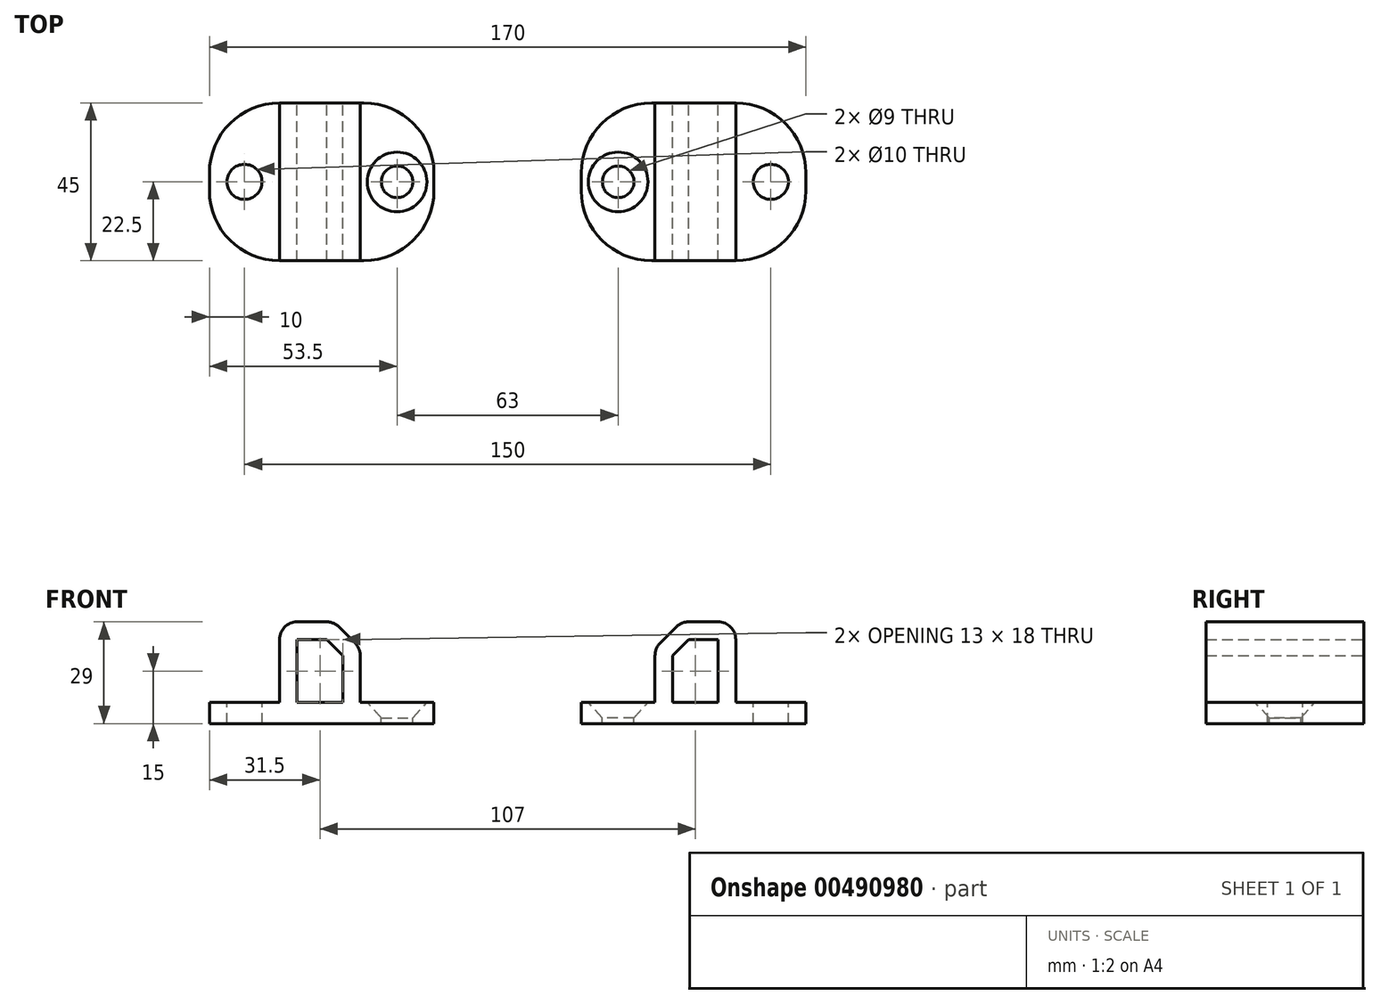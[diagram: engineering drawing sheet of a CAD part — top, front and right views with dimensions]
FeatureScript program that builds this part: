
annotation { "Feature Type Name" : "Feature", "Feature Type Description" : "" }
export const myFeature = defineFeature(function(context is Context, id is Id, definition is map)
    precondition{}
    {
        {
            var Q0;
            Q0=qCreatedBy(makeId("Front.planeOp"),FACE);
            cPlane(context, id + "F0", {"entities" : qUnion([Q0]), "cplaneType" : CPlaneType.OFFSET, "offset" : 15 * mm, "oppositeDirection" : true, "width" : 150 * mm, "height" : 150 * mm});
        }
        {
            var Q0;
            Q0=qCreatedBy(makeId("Top.planeOp"),FACE);
            cPlane(context, id + "F1", {"entities" : qUnion([Q0]), "cplaneType" : CPlaneType.OFFSET, "offset" : 6 * mm, "width" : 150 * mm, "height" : 150 * mm});
        }
        {
            var Q0;
            Q0=qCreatedBy(makeId("Front.planeOp"),FACE);
            var sketch = newSketch(context, id + "F2", { "sketchPlane" : qUnion([Q0])});
            skLineSegment(sketch, "E0", {"start": v(-131, 137) * mm, "end": v(0, 137) * mm});
            skLineSegment(sketch, "E1", {"start": v(-131, 6) * mm, "end": v(0, 6) * mm});
            skCircle(sketch, "E2", {"center": v(-65.5, 71.5) * mm, "radius": 55 * mm});
            skCircle(sketch, "E3", {"center": v(-14.23, 20.23) * mm, "radius": 5 * mm});
            skLineSegment(sketch, "E4", {"start": v(-131, 137) * mm, "end": v(-131, 6) * mm});
            skLineSegment(sketch, "E5", {"start": v(0, 137) * mm, "end": v(0, 6) * mm});
            skSolve(sketch);
        }
        {
            var Q0;
            Q0=qCreatedBy(makeId("Front.planeOp"),FACE);
            var sketch = newSketch(context, id + "F3", { "sketchPlane" : qUnion([Q0])});
            skLineSegment(sketch, "E6", {"start": v(0, 0) * mm, "end": v(-44, 0) * mm});
            skLineSegment(sketch, "E7", {"start": v(0, 0) * mm, "end": v(20, 0) * mm});
            skLineSegment(sketch, "E8", {"start": v(20, 0) * mm, "end": v(20, 6) * mm});
            skLineSegment(sketch, "E9", {"start": v(20, 6) * mm, "end": v(-44, 6) * mm});
            skLineSegment(sketch, "E10", {"start": v(-44, 6) * mm, "end": v(-44, 0) * mm});
            skPoint(sketch, "E11", {"position": v(-65.5, 71.5) * mm});
            skPoint(sketch, "E12", {"position": v(0, 6) * mm});
            skSolve(sketch);
        }
        {
            var Q0;
            Q0=qCreatedBy(id+"F0.planeOp",FACE);
            var sketch = newSketch(context, id + "F4", { "sketchPlane" : qUnion([Q0])});
            skPoint(sketch, "E13", {"position": v(0, 6) * mm});
            skLineSegment(sketch, "E14", {"start": v(0, 6) * mm, "end": v(0, 29) * mm});
            skLineSegment(sketch, "E15", {"start": v(0, 29) * mm, "end": v(-15.5, 29) * mm});
            skLineSegment(sketch, "E16", {"start": v(0, 6) * mm, "end": v(-23, 6) * mm});
            skLineSegment(sketch, "E17", {"start": v(-23, 6) * mm, "end": v(-23, 21.5) * mm});
            skLineSegment(sketch, "E18", {"start": v(-23, 21.5) * mm, "end": v(-15.5, 29) * mm});
            skLineSegment(sketch, "E19.0", {"start": v(-5, 24) * mm, "end": v(-13.43, 24) * mm});
            skLineSegment(sketch, "E19.1", {"start": v(-18, 19.43) * mm, "end": v(-13.43, 24) * mm});
            skLineSegment(sketch, "E20", {"start": v(-18, 19.43) * mm, "end": v(-18, 6) * mm});
            skLineSegment(sketch, "E21", {"start": v(-5, 24) * mm, "end": v(-5, 6) * mm});
            skSolve(sketch);
        }
        {
            var Q0;
            Q0=qCreatedBy(id+"F1.planeOp",FACE);
            var sketch = newSketch(context, id + "F5", { "sketchPlane" : qUnion([Q0])});
            skPoint(sketch, "E22", {"position": v(-44, 0) * mm});
            skLineSegment(sketch, "E23", {"start": v(-44, -5) * mm, "end": v(20, -5) * mm});
            skLineSegment(sketch, "E24", {"start": v(-44, 40) * mm, "end": v(20, 40) * mm});
            skLineSegment(sketch, "E25", {"start": v(-44, 40) * mm, "end": v(-44, -5) * mm});
            skLineSegment(sketch, "E26", {"start": v(20, 40) * mm, "end": v(20, -5) * mm});
            skPoint(sketch, "E27", {"position": v(-23, 15) * mm});
            skPoint(sketch, "E28", {"position": v(0, 15) * mm});
            skPoint(sketch, "E29", {"position": v(-33.5, 15) * mm});
            skPoint(sketch, "E30", {"position": v(10, 15) * mm});
            skLineSegment(sketch, "E31", {"start": v(-33.5, 15) * mm, "end": v(-33.5, 20) * mm});
            skLineSegment(sketch, "E32", {"start": v(10, 15) * mm, "end": v(10, 20) * mm});
            skPoint(sketch, "E33", {"position": v(-33.5, 17.5) * mm});
            skPoint(sketch, "E34", {"position": v(10, 17.5) * mm});
            skSolve(sketch);
        }
        {
            var Q0;
            Q0=makeQuery(id+"F3.imprint","IMPRINT",FACE,{"disambiguationData":[TD([[makeQuery(id+"F3.imprint","IMPRINT",EDGE,{"derivedFrom":sQuery(id+"F3.wireOp",EDGE,"E6")}),-1.0]])]});
            var Q1;
            {var subQ1=sQuery(id+"F3.wireOp",EDGE,"vLAY5ACS-sNxU-jbY8-E00p-dKXXEb0bLBcx");Q1=makeQuery(id+"F3.imprint","IMPRINT",FACE,{"disambiguationData":[TD([[makeQuery(id+"F3.imprint","IMPRINT",EDGE,{"derivedFrom":subQ1}),-1.0]])]});}
            extrude(context, id + "F6", {"entities" : qUnion([Q0, Q1]), "depth" : 5 * mm});
        }
        {
            var Q0;
            Q0=makeQuery(id+"F4.imprint","IMPRINT",FACE,{"disambiguationData":[TD([[makeQuery(id+"F4.imprint","IMPRINT",EDGE,{"derivedFrom":sQuery(id+"F4.wireOp",EDGE,"E14")}),1.0]])]});
            extrude(context, id + "F7", {"entities" : qUnion([Q0]), "operationType" : NewBodyOperationType.ADD, "depth" : 20 * mm});
        }
        {
            var Q0;
            Q0=makeQuery(id+"F3.imprint","IMPRINT",FACE,{"disambiguationData":[TD([[makeQuery(id+"F3.imprint","IMPRINT",EDGE,{"derivedFrom":sQuery(id+"F3.wireOp",EDGE,"E6")}),-1.0]])]});
            extrude(context, id + "F8", {"entities" : qUnion([Q0]), "operationType" : NewBodyOperationType.ADD, "oppositeDirection" : true, "depth" : 40 * mm});
        }
        {
            var Q0;
            Q0=makeQuery(id+"F4.imprint","IMPRINT",FACE,{"disambiguationData":[TD([[makeQuery(id+"F4.imprint","IMPRINT",EDGE,{"derivedFrom":sQuery(id+"F4.wireOp",EDGE,"E14")}),1.0]])]});
            extrude(context, id + "F9", {"entities" : qUnion([Q0]), "operationType" : NewBodyOperationType.ADD, "oppositeDirection" : true, "depth" : 25 * mm});
        }
        {
            var Q0;
            Q0=makeQuery(id+"F9.opExtrude","SWEPT_EDGE",EDGE,{"disambiguationData":[OSD([sQuery(id+"F4.wireOp",EDGE,"E15"),sQuery(id+"F4.wireOp",EDGE,"E18")])]});
            var Q1;
            Q1=makeQuery(id+"F9.opExtrude","SWEPT_EDGE",EDGE,{"disambiguationData":[OSD([sQuery(id+"F4.wireOp",EDGE,"E17"),sQuery(id+"F4.wireOp",EDGE,"E18")])]});
            var Q2;
            Q2=makeQuery(id+"F9.opExtrude","SWEPT_EDGE",EDGE,{"disambiguationData":[OSD([sQuery(id+"F4.wireOp",EDGE,"E14"),sQuery(id+"F4.wireOp",EDGE,"E15")])]});
            var Q3;
            Q3=makeQuery(id+"F6.opExtrude","SWEPT_EDGE",EDGE,{"disambiguationData":[OSD([sQuery(id+"F3.wireOp",EDGE,"expGc7vn-VuKl-lWMZ-9Cwi-WcoAKyNdcV4D"),sQuery(id+"F3.wireOp",EDGE,"TVmZxhZF-jG0O-ZxqZ-yS1S-OARo9sJLRPMk")])]});
            var Q4;
            Q4=makeQuery(id+"F6.opExtrude","SWEPT_EDGE",EDGE,{"disambiguationData":[OSD([sQuery(id+"F3.wireOp",EDGE,"vLAY5ACS-sNxU-jbY8-E00p-dKXXEb0bLBcx"),sQuery(id+"F3.wireOp",EDGE,"TVmZxhZF-jG0O-ZxqZ-yS1S-OARo9sJLRPMk")])]});
            var Q5;
            Q5=makeQuery(id+"F6.opExtrude","SWEPT_EDGE",EDGE,{"disambiguationData":[OSD([sQuery(id+"F3.wireOp",EDGE,"MFwybBEB-61fw-xvZ8-WMQO-FsddWkyA68gy"),sQuery(id+"F3.wireOp",EDGE,"expGc7vn-VuKl-lWMZ-9Cwi-WcoAKyNdcV4D")])]});
            fillet(context, id + "F10", {"entities" : qUnion([Q0, Q1, Q2, Q3, Q4, Q5]), "radius" : 5 * mm, "tangentPropagation" : true, "allowEdgeOverflow" : false});
        }
        {
            var Q0;
            Q0=makeQuery(id+"F6.opExtrude","CAP_EDGE",EDGE,{"disambiguationData":[OSD([sQuery(id+"F3.wireOp",EDGE,"E8")])],"isStart":false});
            var Q1;
            Q1=makeQuery(id+"F8.opExtrude","CAP_EDGE",EDGE,{"disambiguationData":[OSD([sQuery(id+"F3.wireOp",EDGE,"E8")])],"isStart":false});
            var Q2;
            Q2=makeQuery(id+"F8.opExtrude","CAP_EDGE",EDGE,{"disambiguationData":[OSD([sQuery(id+"F3.wireOp",EDGE,"E10")])],"isStart":false});
            var Q3;
            Q3=makeQuery(id+"F6.opExtrude","CAP_EDGE",EDGE,{"disambiguationData":[OSD([sQuery(id+"F3.wireOp",EDGE,"E10")])],"isStart":false});
            fillet(context, id + "F11", {"entities" : qUnion([Q0, Q1, Q2, Q3]), "radius" : 20 * mm, "tangentPropagation" : true, "allowEdgeOverflow" : false});
        }
        {
            var Q0;
            Q0=sQuery(id+"F5.wireOp",VERTEX,"E33");
            var Q1;
            Q1=makeQuery(id+"F6.opExtrude","SWEPT_BODY",BODY,{"disambiguationData":[OSD([sQuery(id+"F3.wireOp",EDGE,"E6"),sQuery(id+"F3.wireOp",EDGE,"E7"),sQuery(id+"F3.wireOp",EDGE,"E8"),sQuery(id+"F3.wireOp",EDGE,"E9"),sQuery(id+"F3.wireOp",EDGE,"E10"),sQuery(id+"F3.wireOp",EDGE,"vLAY5ACS-sNxU-jbY8-E00p-dKXXEb0bLBcx"),sQuery(id+"F3.wireOp",EDGE,"MFwybBEB-61fw-xvZ8-WMQO-FsddWkyA68gy"),sQuery(id+"F3.wireOp",EDGE,"expGc7vn-VuKl-lWMZ-9Cwi-WcoAKyNdcV4D"),sQuery(id+"F3.wireOp",EDGE,"TVmZxhZF-jG0O-ZxqZ-yS1S-OARo9sJLRPMk"),sQuery(id+"F3.wireOp",EDGE,"2V1tZlT7-vU7z-hhUq-sSMV-m2txzCuS0XXM")])]});
            hole(context, id + "F12", {"style" : HoleStyle.C_SINK, "endStyle" : HoleEndStyle.BLIND, "holeDiameter" : 9 * mm, "cSinkDiameter" : 17 * mm, "cSinkAngle" : 85.3 * degree, "holeDepth" : 8 * mm, "isTappedThrough" : true, "tappedDepth" : 12 * mm, "tapClearance" : 3, "locations" : qUnion([Q0]), "scope" : qUnion([Q1])});
        }
        {
            var Q0;
            Q0=sQuery(id+"F5.wireOp",VERTEX,"E34");
            var Q1;
            Q1=makeQuery(id+"F6.opExtrude","SWEPT_BODY",BODY,{"disambiguationData":[OSD([sQuery(id+"F3.wireOp",EDGE,"E6"),sQuery(id+"F3.wireOp",EDGE,"E7"),sQuery(id+"F3.wireOp",EDGE,"E8"),sQuery(id+"F3.wireOp",EDGE,"E9"),sQuery(id+"F3.wireOp",EDGE,"E10"),sQuery(id+"F3.wireOp",EDGE,"vLAY5ACS-sNxU-jbY8-E00p-dKXXEb0bLBcx"),sQuery(id+"F3.wireOp",EDGE,"MFwybBEB-61fw-xvZ8-WMQO-FsddWkyA68gy"),sQuery(id+"F3.wireOp",EDGE,"expGc7vn-VuKl-lWMZ-9Cwi-WcoAKyNdcV4D"),sQuery(id+"F3.wireOp",EDGE,"TVmZxhZF-jG0O-ZxqZ-yS1S-OARo9sJLRPMk"),sQuery(id+"F3.wireOp",EDGE,"2V1tZlT7-vU7z-hhUq-sSMV-m2txzCuS0XXM")])]});
            hole(context, id + "F13", {"style" : HoleStyle.SIMPLE, "endStyle" : HoleEndStyle.BLIND, "holeDiameter" : 10 * mm, "holeDepth" : 8 * mm, "isTappedThrough" : true, "tappedDepth" : 12 * mm, "tapClearance" : 3, "locations" : qUnion([Q0]), "scope" : qUnion([Q1])});
        }
        {
            var Q0;
            Q0=qCreatedBy(makeId("Right.planeOp"),FACE);
            cPlane(context, id + "F14", {"entities" : qUnion([Q0]), "cplaneType" : CPlaneType.OFFSET, "offset" : 65 * mm, "oppositeDirection" : true, "width" : 150 * mm, "height" : 150 * mm});
        }
        {
            var Q0;
            Q0=makeQuery(id+"F6.opExtrude","SWEPT_BODY",BODY,{"disambiguationData":[OSD([sQuery(id+"F3.wireOp",EDGE,"E6"),sQuery(id+"F3.wireOp",EDGE,"E7"),sQuery(id+"F3.wireOp",EDGE,"E8"),sQuery(id+"F3.wireOp",EDGE,"E9"),sQuery(id+"F3.wireOp",EDGE,"E10"),sQuery(id+"F3.wireOp",EDGE,"vLAY5ACS-sNxU-jbY8-E00p-dKXXEb0bLBcx"),sQuery(id+"F3.wireOp",EDGE,"MFwybBEB-61fw-xvZ8-WMQO-FsddWkyA68gy"),sQuery(id+"F3.wireOp",EDGE,"expGc7vn-VuKl-lWMZ-9Cwi-WcoAKyNdcV4D"),sQuery(id+"F3.wireOp",EDGE,"TVmZxhZF-jG0O-ZxqZ-yS1S-OARo9sJLRPMk"),sQuery(id+"F3.wireOp",EDGE,"2V1tZlT7-vU7z-hhUq-sSMV-m2txzCuS0XXM")])]});
            var Q1;
            Q1=qCreatedBy(id+"F14.planeOp",FACE);
            mirror(context, id + "F15", {"entities" : qUnion([Q0]), "mirrorPlane" : qUnion([Q1])});
        }
    });
